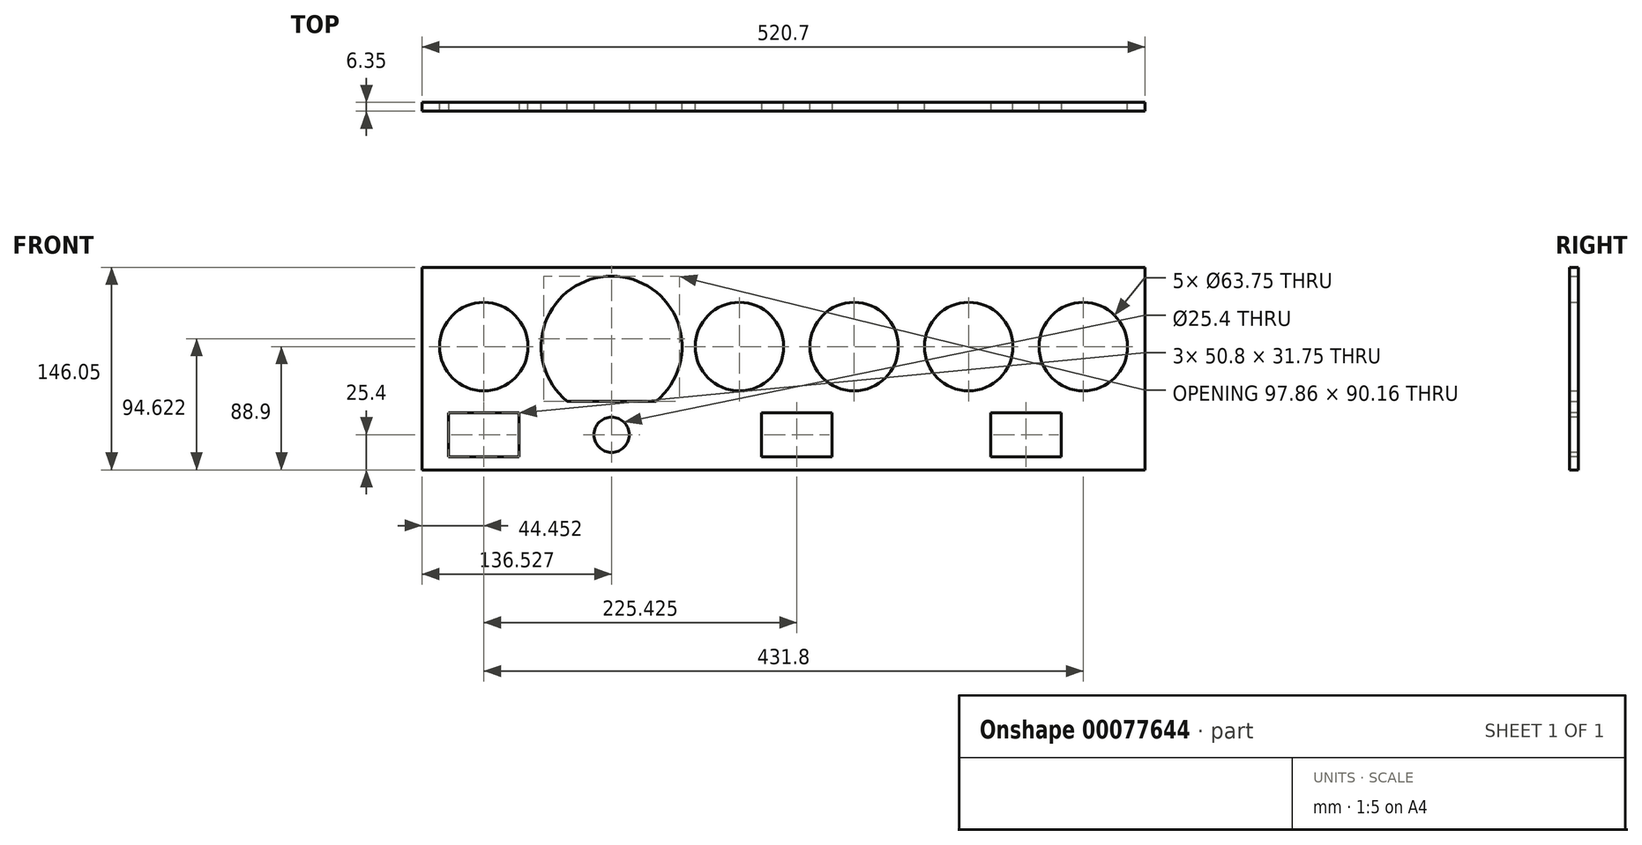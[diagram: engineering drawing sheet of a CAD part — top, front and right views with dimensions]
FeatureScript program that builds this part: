
annotation { "Feature Type Name" : "Feature", "Feature Type Description" : "" }
export const myFeature = defineFeature(function(context is Context, id is Id, definition is map)
    precondition{}
    {
        {
            var Q0;
            Q0=qCreatedBy(makeId("Front.planeOp"),FACE);
            var sketch = newSketch(context, id + "F0", { "sketchPlane" : qUnion([Q0])});
            skPoint(sketch, "E0.middle", {"position": v(0, 0) * mm});
            skLineSegment(sketch, "E1.bottom", {"start": v(-260.34, 146.05) * mm, "end": v(260.36, 146.05) * mm});
            skLineSegment(sketch, "E1.top", {"start": v(-260.34, 0) * mm, "end": v(260.36, 0) * mm});
            skLineSegment(sketch, "E1.left", {"start": v(-260.34, 146.05) * mm, "end": v(-260.34, 0) * mm});
            skLineSegment(sketch, "E1.right", {"start": v(260.36, 146.05) * mm, "end": v(260.36, 0) * mm});
            skCircle(sketch, "E2", {"center": v(-215.89, 88.9) * mm, "radius": 31.88 * mm});
            skCircle(sketch, "E3", {"center": v(-123.81, 88.9) * mm, "radius": 50.8 * mm});
            skCircle(sketch, "E4", {"center": v(-31.74, 88.9) * mm, "radius": 31.88 * mm});
            skCircle(sketch, "E5", {"center": v(50.81, 88.9) * mm, "radius": 31.88 * mm});
            skCircle(sketch, "E6", {"center": v(133.36, 88.9) * mm, "radius": 31.88 * mm});
            skCircle(sketch, "E7", {"center": v(215.91, 88.9) * mm, "radius": 31.88 * mm});
            skLineSegment(sketch, "E8", {"start": v(-155.93, 49.54) * mm, "end": v(-91.7, 49.54) * mm});
            skSolve(sketch);
        }
        {
            var Q0;
            Q0=makeQuery(id+"F0.imprint","IMPRINT",FACE,{"disambiguationData":[TD([[makeQuery(id+"F0.imprint","IMPRINT",EDGE,{"derivedFrom":sQuery(id+"F0.wireOp",EDGE,"E1.bottom")}),-1.0]])]});
            var Q1;
            Q1=makeQuery(id+"F0.imprint","IMPRINT",FACE,{"disambiguationData":[TD([[makeQuery(id+"F0.imprint","IMPRINT",EDGE,{"derivedFrom":sQuery(id+"F0.wireOp",EDGE,"E0.top")}),1.0]])]});
            extrude(context, id + "F1", {"entities" : qUnion([Q0, Q1]), "depth" : 6.35 * mm});
        }
        {
            var Q0;
            {var subQ0=sQuery(id+"F0.wireOp",EDGE,"E8");Q0=makeQuery(id+"F0.imprint","IMPRINT",FACE,{"disambiguationData":[TD([[makeQuery(id+"F0.imprint","IMPRINT",EDGE,{"derivedFrom":subQ0}),-1.0]])]});}
            extrude(context, id + "F2", {"entities" : qUnion([Q0]), "operationType" : NewBodyOperationType.ADD, "depth" : 6.35 * mm});
        }
        {
            var Q0;
            Q0=makeQuery(id+"F1.opExtrude","CAP_FACE",FACE,{"disambiguationData":[OSD([sQuery(id+"F0.wireOp",EDGE,"E0.bottom"),sQuery(id+"F0.wireOp",EDGE,"E0.top"),sQuery(id+"F0.wireOp",EDGE,"E0.left"),sQuery(id+"F0.wireOp",EDGE,"E0.right"),sQuery(id+"F0.wireOp",EDGE,"E1.bottom"),sQuery(id+"F0.wireOp",EDGE,"E2"),sQuery(id+"F0.wireOp",EDGE,"E3"),sQuery(id+"F0.wireOp",EDGE,"E4"),sQuery(id+"F0.wireOp",EDGE,"E5"),sQuery(id+"F0.wireOp",EDGE,"E6"),sQuery(id+"F0.wireOp",EDGE,"E7")])],"isStart":false});
            var sketch = newSketch(context, id + "F3", { "sketchPlane" : qUnion([Q0])});
            skCircle(sketch, "E9", {"center": v(-215.89, 25.4) * mm, "radius": 10.1 * mm});
            skCircle(sketch, "E10", {"center": v(9.54, 25.4) * mm, "radius": 9.35 * mm});
            skCircle(sketch, "E11", {"center": v(174.64, 25.4) * mm, "radius": 9.4 * mm});
            skSolve(sketch);
        }
        {
            var Q0;
            Q0 = qSketchRegion(id + "F3", true);
            extrude(context, id + "F4", {"entities" : qUnion([Q0]), "operationType" : NewBodyOperationType.REMOVE, "oppositeDirection" : true, "depth" : 25.4 * mm});
        }
        {
            var Q0;
            Q0=makeQuery(id+"F1.opExtrude","CAP_FACE",FACE,{"disambiguationData":[OSD([sQuery(id+"F0.wireOp",EDGE,"E0.bottom"),sQuery(id+"F0.wireOp",EDGE,"E0.top"),sQuery(id+"F0.wireOp",EDGE,"E0.left"),sQuery(id+"F0.wireOp",EDGE,"E0.right"),sQuery(id+"F0.wireOp",EDGE,"E1.bottom"),sQuery(id+"F0.wireOp",EDGE,"E2"),sQuery(id+"F0.wireOp",EDGE,"E3"),sQuery(id+"F0.wireOp",EDGE,"E4"),sQuery(id+"F0.wireOp",EDGE,"E5"),sQuery(id+"F0.wireOp",EDGE,"E6"),sQuery(id+"F0.wireOp",EDGE,"E7")])],"isStart":false});
            var sketch = newSketch(context, id + "F5", { "sketchPlane" : qUnion([Q0])});
            skPoint(sketch, "E12.middle", {"position": v(-123.81, 88.9) * mm});
            skCircle(sketch, "E13", {"center": v(-155.56, 120.65) * mm, "radius": 2.41 * mm});
            skCircle(sketch, "E14", {"center": v(-92.06, 120.65) * mm, "radius": 2.41 * mm});
            skCircle(sketch, "E15", {"center": v(-92.06, 57.15) * mm, "radius": 2.41 * mm});
            skCircle(sketch, "E16", {"center": v(-155.56, 57.15) * mm, "radius": 2.41 * mm});
            skSolve(sketch);
        }
        {
            var Q0;
            Q0 = qSketchRegion(id + "F5", true);
            extrude(context, id + "F6", {"entities" : qUnion([Q0]), "operationType" : NewBodyOperationType.REMOVE, "oppositeDirection" : true, "depth" : 25.4 * mm});
        }
        {
            var Q0;
            Q0=makeQuery(id+"F1.opExtrude","CAP_FACE",FACE,{"disambiguationData":[OSD([sQuery(id+"F0.wireOp",EDGE,"E0.bottom"),sQuery(id+"F0.wireOp",EDGE,"E0.top"),sQuery(id+"F0.wireOp",EDGE,"E0.left"),sQuery(id+"F0.wireOp",EDGE,"E0.right"),sQuery(id+"F0.wireOp",EDGE,"E1.bottom"),sQuery(id+"F0.wireOp",EDGE,"E2"),sQuery(id+"F0.wireOp",EDGE,"E3"),sQuery(id+"F0.wireOp",EDGE,"E4"),sQuery(id+"F0.wireOp",EDGE,"E5"),sQuery(id+"F0.wireOp",EDGE,"E6"),sQuery(id+"F0.wireOp",EDGE,"E7")])],"isStart":false});
            var sketch = newSketch(context, id + "F7", { "sketchPlane" : qUnion([Q0])});
            skLineSegment(sketch, "E17.bottom", {"start": v(-273.05, 146.05) * mm, "end": v(-266.7, 146.05) * mm});
            skLineSegment(sketch, "E17.top", {"start": v(-273.05, 139.7) * mm, "end": v(-266.7, 139.7) * mm});
            skLineSegment(sketch, "E17.left", {"start": v(-273.05, 146.05) * mm, "end": v(-273.05, 139.7) * mm});
            skLineSegment(sketch, "E17.right", {"start": v(-266.7, 146.05) * mm, "end": v(-266.7, 139.7) * mm});
            skLineSegment(sketch, "E18.bottom", {"start": v(273.05, 146.05) * mm, "end": v(266.7, 146.05) * mm});
            skLineSegment(sketch, "E18.top", {"start": v(273.05, 139.7) * mm, "end": v(266.7, 139.7) * mm});
            skLineSegment(sketch, "E18.left", {"start": v(273.05, 146.05) * mm, "end": v(273.05, 139.7) * mm});
            skLineSegment(sketch, "E18.right", {"start": v(266.7, 146.05) * mm, "end": v(266.7, 139.7) * mm});
            skSolve(sketch);
        }
        {
            var Q0;
            Q0 = qSketchRegion(id + "F7", true);
            extrude(context, id + "F8", {"entities" : qUnion([Q0]), "operationType" : NewBodyOperationType.REMOVE, "oppositeDirection" : true, "depth" : 25.4 * mm});
        }
        {
            var Q0;
            Q0=makeQuery(id+"F1.opExtrude","CAP_FACE",FACE,{"disambiguationData":[OSD([sQuery(id+"F0.wireOp",EDGE,"E1.bottom"),sQuery(id+"F0.wireOp",EDGE,"E1.top"),sQuery(id+"F0.wireOp",EDGE,"E1.left"),sQuery(id+"F0.wireOp",EDGE,"E1.right"),sQuery(id+"F0.wireOp",EDGE,"E2"),sQuery(id+"F0.wireOp",EDGE,"E3"),sQuery(id+"F0.wireOp",EDGE,"E4"),sQuery(id+"F0.wireOp",EDGE,"E5"),sQuery(id+"F0.wireOp",EDGE,"E6"),sQuery(id+"F0.wireOp",EDGE,"E7")])],"isStart":false});
            var sketch = newSketch(context, id + "F9", { "sketchPlane" : qUnion([Q0])});
            skLineSegment(sketch, "E19.bottom", {"start": v(-190.49, 41.28) * mm, "end": v(-241.29, 41.28) * mm});
            skLineSegment(sketch, "E19.top", {"start": v(-190.49, 9.53) * mm, "end": v(-241.29, 9.53) * mm});
            skLineSegment(sketch, "E19.left", {"start": v(-190.49, 41.28) * mm, "end": v(-190.49, 9.53) * mm});
            skLineSegment(sketch, "E19.right", {"start": v(-241.29, 41.28) * mm, "end": v(-241.29, 9.53) * mm});
            skPoint(sketch, "E19.middle", {"position": v(-215.89, 25.4) * mm});
            skPoint(sketch, "E20.middle", {"position": v(-123.83, 25.4) * mm});
            skLineSegment(sketch, "E21.bottom", {"start": v(34.94, 41.28) * mm, "end": v(-15.86, 41.28) * mm});
            skLineSegment(sketch, "E21.top", {"start": v(34.94, 9.53) * mm, "end": v(-15.86, 9.53) * mm});
            skLineSegment(sketch, "E21.left", {"start": v(34.94, 41.28) * mm, "end": v(34.94, 9.53) * mm});
            skLineSegment(sketch, "E21.right", {"start": v(-15.86, 41.28) * mm, "end": v(-15.86, 9.53) * mm});
            skPoint(sketch, "E21.middle", {"position": v(9.54, 25.4) * mm});
            skLineSegment(sketch, "E22.bottom", {"start": v(200.04, 41.28) * mm, "end": v(149.24, 41.28) * mm});
            skLineSegment(sketch, "E22.top", {"start": v(200.04, 9.53) * mm, "end": v(149.24, 9.53) * mm});
            skLineSegment(sketch, "E22.left", {"start": v(200.04, 41.28) * mm, "end": v(200.04, 9.53) * mm});
            skLineSegment(sketch, "E22.right", {"start": v(149.24, 41.28) * mm, "end": v(149.24, 9.53) * mm});
            skPoint(sketch, "E22.middle", {"position": v(174.64, 25.4) * mm});
            skSolve(sketch);
        }
        {
            var Q0;
            Q0 = qSketchRegion(id + "F9", true);
            extrude(context, id + "F10", {"entities" : qUnion([Q0]), "operationType" : NewBodyOperationType.REMOVE, "oppositeDirection" : true, "depth" : 25.4 * mm});
        }
        {
            var Q0;
            Q0=makeQuery(id+"F3.imprint","IMPRINT",FACE,{"disambiguationData":[TD([[makeQuery(id+"F3.imprint","IMPRINT",EDGE,{"derivedFrom":sQuery(id+"F3.wireOp",EDGE,"E9")}),-1.0]])]});
            var sketch = newSketch(context, id + "F11", { "sketchPlane" : qUnion([Q0])});
            skCircle(sketch, "E23", {"center": v(-123.81, 25.4) * mm, "radius": 12.7 * mm});
            skSolve(sketch);
        }
        {
            var Q0;
            Q0=makeQuery(id+"F11.imprint","IMPRINT",FACE,{"disambiguationData":[TD([[makeQuery(id+"F11.imprint","IMPRINT",EDGE,{"derivedFrom":sQuery(id+"F11.wireOp",EDGE,"E23")}),1.0]])]});
            extrude(context, id + "F12", {"entities" : qUnion([Q0]), "operationType" : NewBodyOperationType.REMOVE, "endBound" : BoundingType.SYMMETRIC, "oppositeDirection" : true, "depth" : 25.4 * mm});
        }
    });
